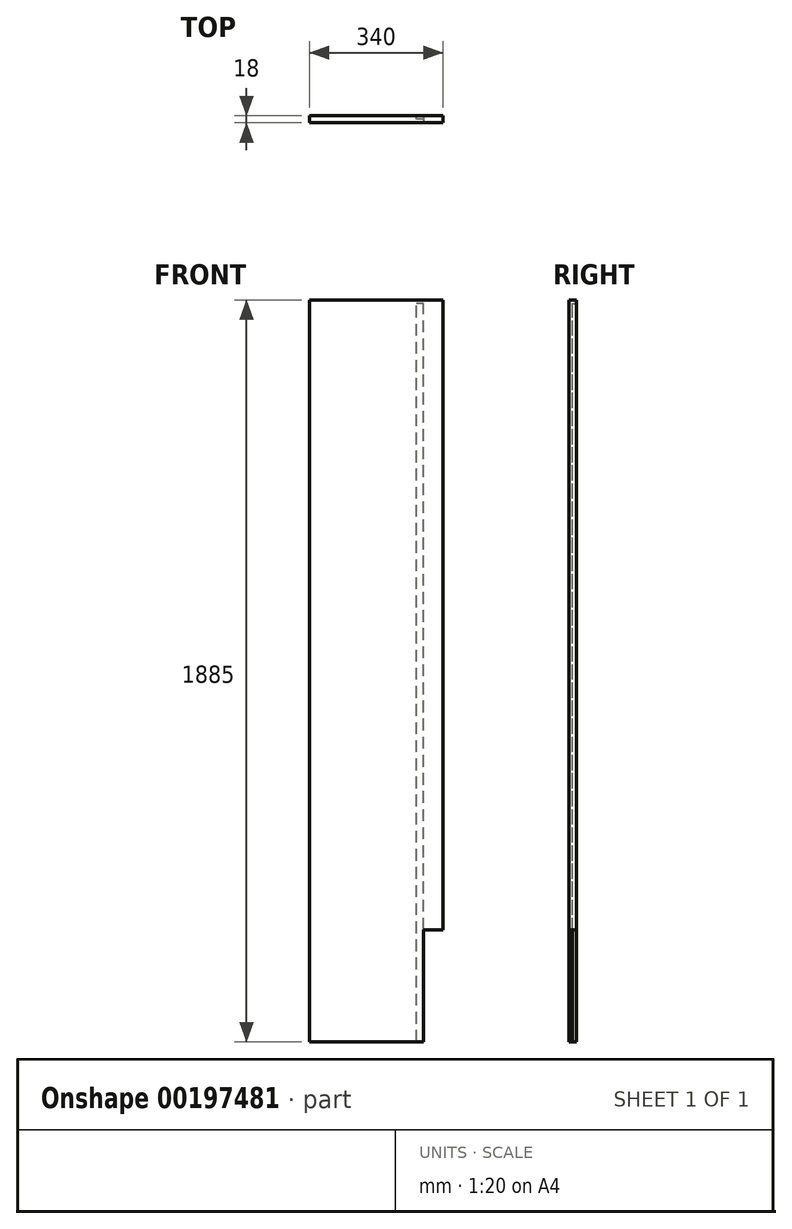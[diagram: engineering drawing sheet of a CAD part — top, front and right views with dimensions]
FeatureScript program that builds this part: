
annotation { "Feature Type Name" : "Feature", "Feature Type Description" : "" }
export const myFeature = defineFeature(function(context is Context, id is Id, definition is map)
    precondition{}
    {
        {
            var Q0;
            Q0=qCreatedBy(makeId("Front.planeOp"),FACE);
            var sketch = newSketch(context, id + "F0", { "sketchPlane" : qUnion([Q0])});
            skLineSegment(sketch, "E0.bottom", {"start": v(170, 942.5) * mm, "end": v(-170, 942.5) * mm});
            skLineSegment(sketch, "E0.top", {"start": v(170, -942.5) * mm, "end": v(-170, -942.5) * mm});
            skLineSegment(sketch, "E0.left", {"start": v(170, 942.5) * mm, "end": v(170, -942.5) * mm});
            skLineSegment(sketch, "E0.right", {"start": v(-170, 942.5) * mm, "end": v(-170, -942.5) * mm});
            skPoint(sketch, "E0.middle", {"position": v(0, 0) * mm});
            skSolve(sketch);
        }
        {
            var Q0;
            Q0=qSketchRegion(id+"F0",true);
            extrude(context, id + "F1", {"entities" : qUnion([Q0]), "depth" : 18 * mm});
        }
        {
            var Q0;
            Q0=makeQuery(id+"F1.opExtrude","CAP_FACE",FACE,{"disambiguationData":[OSD([sQuery(id+"F0.wireOp",EDGE,"E0.bottom"),sQuery(id+"F0.wireOp",EDGE,"E0.top"),sQuery(id+"F0.wireOp",EDGE,"E0.left"),sQuery(id+"F0.wireOp",EDGE,"E0.right")])],"isStart":false});
            var sketch = newSketch(context, id + "F2", { "sketchPlane" : qUnion([Q0])});
            skLineSegment(sketch, "E1.bottom", {"start": v(170, -942.5) * mm, "end": v(120, -942.5) * mm});
            skLineSegment(sketch, "E1.top", {"start": v(170, -657.5) * mm, "end": v(120, -657.5) * mm});
            skLineSegment(sketch, "E1.left", {"start": v(170, -942.5) * mm, "end": v(170, -657.5) * mm});
            skLineSegment(sketch, "E1.right", {"start": v(120, -942.5) * mm, "end": v(120, -657.5) * mm});
            skSolve(sketch);
        }
        {
            var Q0;
            Q0=qSketchRegion(id+"F2",true);
            extrude(context, id + "F3", {"entities" : qUnion([Q0]), "operationType" : NewBodyOperationType.REMOVE, "oppositeDirection" : true, "depth" : 18 * mm});
        }
        {
            var Q0;
            Q0=makeQuery(id+"F1.opExtrude","CAP_FACE",FACE,{"disambiguationData":[OSD([sQuery(id+"F0.wireOp",EDGE,"E0.bottom"),sQuery(id+"F0.wireOp",EDGE,"E0.top"),sQuery(id+"F0.wireOp",EDGE,"E0.left"),sQuery(id+"F0.wireOp",EDGE,"E0.right")])],"isStart":true});
            var sketch = newSketch(context, id + "F4", { "sketchPlane" : qUnion([Q0])});
            skLineSegment(sketch, "E2.bottom", {"start": v(-120, -942.5) * mm, "end": v(-102, -942.5) * mm});
            skLineSegment(sketch, "E2.top", {"start": v(-120, 933.5) * mm, "end": v(-102, 933.5) * mm});
            skLineSegment(sketch, "E2.left", {"start": v(-120, -942.5) * mm, "end": v(-120, 933.5) * mm});
            skLineSegment(sketch, "E2.right", {"start": v(-102, -942.5) * mm, "end": v(-102, 933.5) * mm});
            skSolve(sketch);
        }
        {
            var Q0;
            Q0=qSketchRegion(id+"F4",true);
            extrude(context, id + "F5", {"entities" : qUnion([Q0]), "operationType" : NewBodyOperationType.REMOVE, "oppositeDirection" : true, "depth" : 9 * mm});
        }
    });
